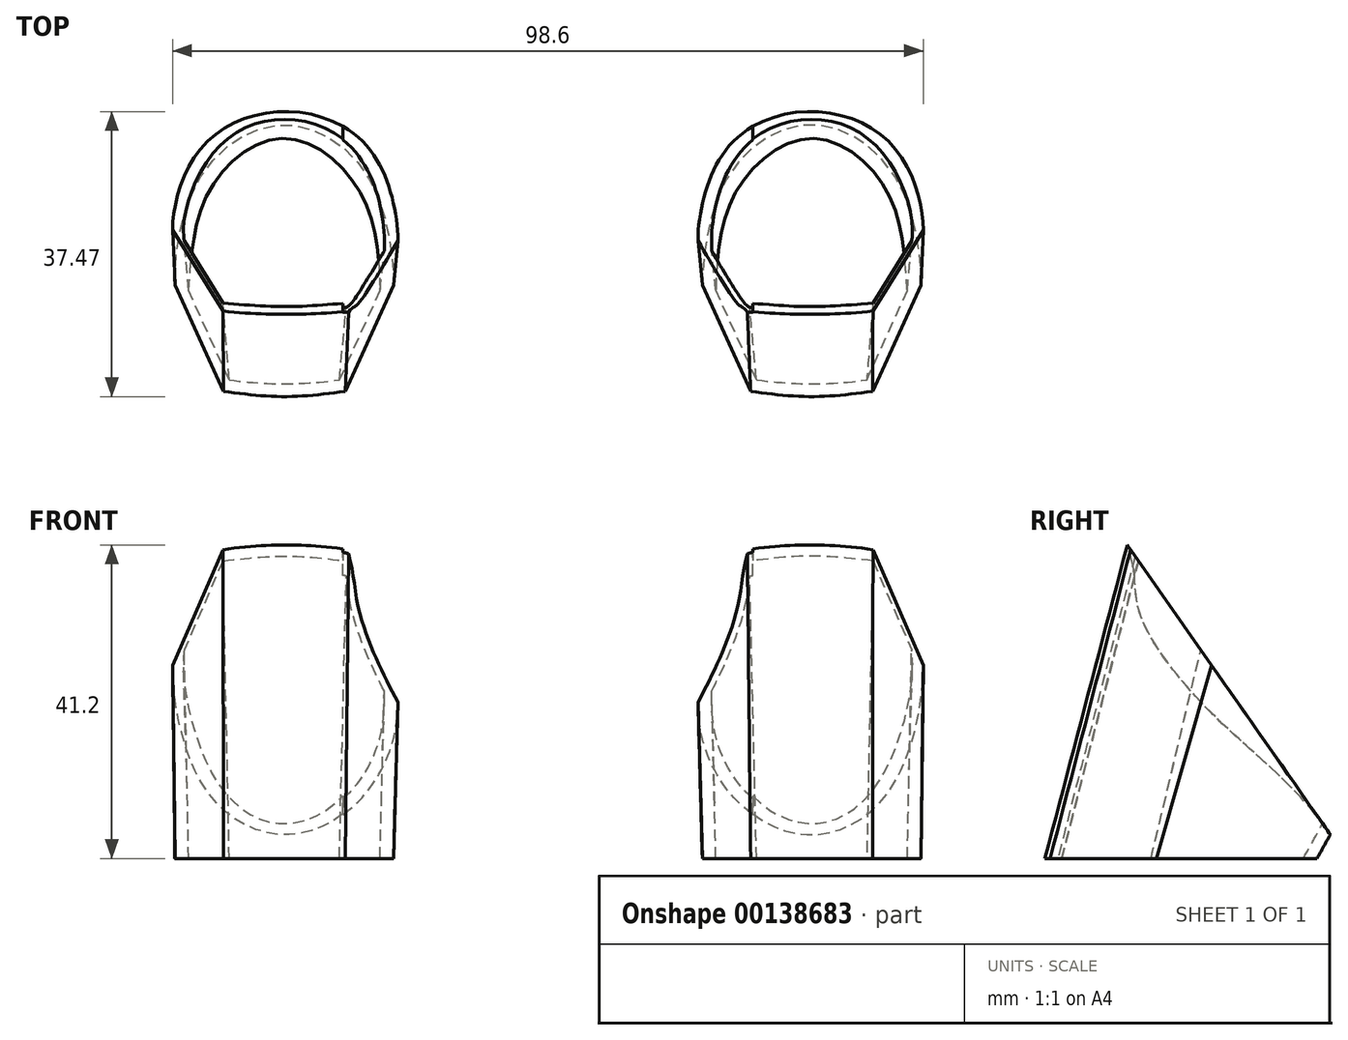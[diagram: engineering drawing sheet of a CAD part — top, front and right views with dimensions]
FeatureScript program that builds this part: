
annotation { "Feature Type Name" : "Feature", "Feature Type Description" : "" }
export const myFeature = defineFeature(function(context is Context, id is Id, definition is map)
    precondition{}
    {
        {
            var Q0;
            Q0=qCreatedBy(makeId("Top.planeOp"),FACE);
            var sketch = newSketch(context, id + "F0", { "sketchPlane" : qUnion([Q0])});
            skLineSegment(sketch, "E0", {"start": v(-1.23, -17.04) * mm, "end": v(5.12, -3.07) * mm});
            skLineSegment(sketch, "E1", {"start": v(-17.23, -17.04) * mm, "end": v(-23.58, -3.07) * mm});
            skPoint(sketch, "E2.2.internal.snap0", {"position": v(-9.23, -17.04) * mm});
            skFitSpline(sketch, "E2", {"points": [v(-23.58, -3.07) * mm, v(-20.66, 10.4) * mm, v(-9.23, 18.01) * mm, v(2.2, 10.4) * mm, v(5.12, -3.07) * mm], "startDerivative": vector(-1.89, 32.45) * mm, "endDerivative": vector(-0.1, -29.67) * mm});
            skFitSpline(sketch, "E3", {"points": [v(-17.23, -17.04) * mm, v(-9.23, -17.71) * mm, v(-1.23, -17.04) * mm], "startDerivative": vector(16.69, -2.01) * mm, "endDerivative": vector(16.69, 2.01) * mm});
            skLineSegment(sketch, "E4", {"start": v(10.38, -21.65) * mm, "end": v(-32.58, -21.65) * mm});
            skLineSegment(sketch, "E5", {"start": v(-40, 21.95) * mm, "end": v(17.74, 21.95) * mm});
            skSolve(sketch);
        }
        {
            var Q0;
            Q0=sQuery(id+"F0.wireOp",EDGE,"E5");
            cPlane(context, id + "F1", {"entities" : qUnion([Q0]), "cplaneType" : CPlaneType.LINE_ANGLE, "offset" : 25.4 * mm, "angle" : 35 * degree, "width" : 152.4 * mm, "height" : 152.4 * mm});
        }
        {
            var Q0;
            Q0=qCreatedBy(id+"F1.planeOp",FACE);
            var sketch = newSketch(context, id + "F2", { "sketchPlane" : qUnion([Q0])});
            skFitSpline(sketch, "E6", {"points": [v(-5.82, 18.4) * mm, v(-1.25, -1.92) * mm, v(9.18, -8.78) * mm, v(19.33, -1.92) * mm, v(23.9, 18.4) * mm], "startDerivative": vector(0, -61.98) * mm, "endDerivative": vector(0, 61.98) * mm});
            skLineSegment(sketch, "E7", {"start": v(-5.82, 18.4) * mm, "end": v(0.79, 36.94) * mm});
            skFitSpline(sketch, "E8", {"points": [v(0.79, 36.94) * mm, v(8.9, 37.7) * mm, v(17.3, 36.94) * mm], "startDerivative": vector(19.24, 3.46) * mm, "endDerivative": vector(17.7, -3.53) * mm});
            skLineSegment(sketch, "E9", {"start": v(23.9, 18.4) * mm, "end": v(17.3, 36.94) * mm});
            skLineSegment(sketch, "E10.0", {"start": v(40, -12.59) * mm, "end": v(-17.74, -12.59) * mm});
            skSolve(sketch);
        }
        {
            var Q0;
            Q0=makeQuery(id+"F0.imprint","IMPRINT",FACE,{"disambiguationData":[TD([[makeQuery(id+"F0.imprint","IMPRINT",EDGE,{"derivedFrom":sQuery(id+"F0.wireOp",EDGE,"E0")}),1.0]])]});
            var Q1;
            Q1=makeQuery(id+"F2.imprint","IMPRINT",FACE,{"disambiguationData":[TD([[makeQuery(id+"F2.imprint","IMPRINT",EDGE,{"derivedFrom":sQuery(id+"F2.wireOp",EDGE,"E6")}),1.0]])]});
            loft(context, id + "F3", {"sheetProfilesArray" : [{ "sheetProfileEntities" : qUnion([Q0]) }, { "sheetProfileEntities" : qUnion([Q1]) }]});
        }
        {
            var Q0;
            Q0=qCreatedBy(makeId("Top.planeOp"),FACE);
            var sketch = newSketch(context, id + "F4", { "sketchPlane" : qUnion([Q0])});
            skFitSpline(sketch, "E11.0.0", {"points": [v(-17.23, -17.04) * mm, v(-14.45, -17.38) * mm, v(-9.23, -18.05) * mm, v(-4.01, -17.38) * mm, v(-1.23, -17.04) * mm]});
            skLineSegment(sketch, "E11.0.1", {"start": v(-1.23, -17.04) * mm, "end": v(5.12, -3.07) * mm});
            skFitSpline(sketch, "E11.0.2", {"points": [v(5.12, -3.07) * mm, v(5.13, -0.6) * mm, v(4.22, 12.05) * mm, v(-9.25, 21.01) * mm, v(-22.6, 11.95) * mm, v(-23.74, -0.37) * mm, v(-23.58, -3.07) * mm]});
            skLineSegment(sketch, "E11.0.3", {"start": v(-23.58, -3.07) * mm, "end": v(-17.23, -17.04) * mm});
            skFitSpline(sketch, "E12", {"points": [v(-16.47, -15.52) * mm, v(-9.46, -16.03) * mm, v(-2, -15.52) * mm], "startDerivative": vector(14.42, -1.9) * mm, "endDerivative": vector(15.64, 1.87) * mm});
            skLineSegment(sketch, "E13", {"start": v(-2, -15.52) * mm, "end": v(3.34, -3.78) * mm});
            skLineSegment(sketch, "E14", {"start": v(-16.47, -15.52) * mm, "end": v(-21.8, -3.78) * mm});
            skFitSpline(sketch, "E15", {"points": [v(-21.8, -3.78) * mm, v(-19.26, 9) * mm, v(-9.23, 16.23) * mm, v(0.8, 9) * mm, v(3.34, -3.78) * mm], "startDerivative": vector(3.68, 44.37) * mm, "endDerivative": vector(1.43, -50.48) * mm});
            skPoint(sketch, "E16.0", {"position": v(-20.66, 10.4) * mm});
            skPoint(sketch, "E17.0", {"position": v(-9.23, 18.01) * mm});
            skPoint(sketch, "E18.0", {"position": v(2.2, 10.4) * mm});
            skSolve(sketch);
        }
        {
            var Q0;
            Q0=qCreatedBy(id+"F1.planeOp",FACE);
            var sketch = newSketch(context, id + "F5", { "sketchPlane" : qUnion([Q0])});
            skLineSegment(sketch, "E19.0", {"start": v(23.9, 18.4) * mm, "end": v(17.3, 36.94) * mm});
            skFitSpline(sketch, "E20.0", {"points": [v(17.83, 38.56) * mm, v(16.45, 38.83) * mm, v(14.96, 39.03) * mm, v(13.36, 39.16) * mm, v(12.65, 39.22) * mm, v(11.9, 39.26) * mm, v(11.14, 39.28) * mm, v(10.44, 39.3) * mm, v(9.71, 39.32) * mm, v(8.96, 39.32) * mm, v(8.22, 39.32) * mm, v(7.52, 39.3) * mm, v(6.85, 39.28) * mm, v(6.13, 39.25) * mm, v(5.42, 39.2) * mm, v(4.74, 39.15) * mm, v(4.01, 39.1) * mm, v(3.29, 39.01) * mm, v(2.56, 38.92) * mm, v(1.8, 38.82) * mm, v(1.04, 38.7) * mm, v(0.25, 38.56) * mm]});
            skFitSpline(sketch, "E21.0", {"points": [v(-6.86, 20.01) * mm, v(-6.86, 19.34) * mm, v(-6.85, 18.65) * mm, v(-6.82, 17.94) * mm, v(-6.8, 17.2) * mm, v(-6.75, 16.45) * mm, v(-6.69, 15.7) * mm, v(-6.62, 14.9) * mm, v(-6.54, 14.1) * mm, v(-6.45, 13.32) * mm, v(-6.35, 12.49) * mm, v(-6.23, 11.68) * mm, v(-6.1, 10.88) * mm, v(-5.95, 10.03) * mm, v(-5.79, 9.21) * mm, v(-5.61, 8.42) * mm, v(-5.42, 7.58) * mm, v(-5.22, 6.77) * mm, v(-4.99, 6) * mm, v(-4.75, 5.19) * mm, v(-4.5, 4.4) * mm, v(-4.22, 3.67) * mm, v(-3.93, 2.9) * mm, v(-3.62, 2.17) * mm, v(-3.28, 1.5) * mm, v(-2.94, 0.78) * mm, v(-2.57, 0.12) * mm, v(-2.18, -0.5) * mm, v(-1.78, -1.1) * mm, v(-1.35, -1.69) * mm, v(-0.9, -2.23) * mm, v(-0.44, -2.76) * mm, v(0.04, -3.26) * mm, v(0.55, -3.72) * mm, v(1.05, -4.17) * mm, v(1.57, -4.57) * mm, v(2.12, -4.94) * mm, v(2.65, -5.3) * mm, v(3.21, -5.63) * mm, v(3.78, -5.9) * mm, v(4.35, -6.18) * mm, v(4.93, -6.41) * mm, v(5.53, -6.6) * mm, v(6.12, -6.79) * mm, v(6.71, -6.93) * mm, v(7.31, -7.02) * mm, v(7.92, -7.12) * mm, v(8.52, -7.16) * mm, v(9.12, -7.16) * mm, v(9.73, -7.16) * mm, v(10.33, -7.12) * mm, v(10.93, -7.02) * mm, v(11.52, -6.93) * mm, v(12.11, -6.79) * mm, v(12.7, -6.6) * mm, v(13.28, -6.42) * mm, v(13.85, -6.18) * mm, v(14.41, -5.9) * mm, v(14.98, -5.63) * mm, v(15.52, -5.3) * mm, v(16.05, -4.94) * mm, v(16.66, -4.52) * mm, v(17.24, -4.05) * mm, v(17.8, -3.52) * mm, v(18.36, -2.98) * mm, v(18.88, -2.4) * mm, v(19.37, -1.76) * mm, v(19.75, -1.27) * mm, v(20.1, -0.76) * mm, v(20.42, -0.22) * mm, v(20.75, 0.31) * mm, v(21.05, 0.88) * mm, v(21.35, 1.5) * mm, v(21.68, 2.17) * mm, v(21.98, 2.9) * mm, v(22.27, 3.67) * mm, v(22.55, 4.4) * mm, v(22.8, 5.19) * mm, v(23.04, 6) * mm, v(23.27, 6.78) * mm, v(23.48, 7.58) * mm, v(23.67, 8.42) * mm, v(23.85, 9.22) * mm, v(24, 10.03) * mm, v(24.15, 10.88) * mm, v(24.3, 11.68) * mm, v(24.41, 12.5) * mm, v(24.51, 13.32) * mm, v(24.61, 14.1) * mm, v(24.7, 14.9) * mm, v(24.76, 15.7) * mm, v(24.82, 16.45) * mm, v(24.87, 17.2) * mm, v(24.9, 17.94) * mm, v(24.93, 18.65) * mm, v(24.94, 19.34) * mm, v(24.94, 20.01) * mm]});
            skLineSegment(sketch, "E22.0", {"start": v(0.79, 36.94) * mm, "end": v(-5.82, 18.4) * mm});
            skFitSpline(sketch, "E23", {"points": [v(17.3, 35.16) * mm, v(8.9, 35.93) * mm, v(1.05, 35.16) * mm], "startDerivative": vector(-16.31, 2.01) * mm, "endDerivative": vector(-16.4, -1.86) * mm});
            skPoint(sketch, "E24.0", {"position": v(9.23, 9.2) * mm});
            skPoint(sketch, "E25.0", {"position": v(8.9, 37.7) * mm});
            skLineSegment(sketch, "E26", {"start": v(1.05, 35.16) * mm, "end": v(-4.04, 20.88) * mm});
            skLineSegment(sketch, "E27", {"start": v(17.3, 35.16) * mm, "end": v(22.38, 20.88) * mm});
            skFitSpline(sketch, "E28", {"points": [v(22.38, 20.88) * mm, v(17.93, -0.52) * mm, v(9.18, -7) * mm, v(0.15, -0.52) * mm, v(-4.04, 20.88) * mm], "startDerivative": vector(6.23, -52.02) * mm, "endDerivative": vector(2.54, 68.04) * mm});
            skPoint(sketch, "E29.0", {"position": v(-1.25, -1.92) * mm});
            skPoint(sketch, "E30.0", {"position": v(9.18, -8.78) * mm});
            skPoint(sketch, "E31.0", {"position": v(19.33, -1.92) * mm});
            skSolve(sketch);
        }
        {
            var Q1;
            Q1=makeQuery(id+"F4.imprint","IMPRINT",FACE,{"disambiguationData":[TD([[makeQuery(id+"F4.imprint","IMPRINT",EDGE,{"derivedFrom":sQuery(id+"F4.wireOp",EDGE,"E12")}),1.0]])]});
            var Q2;
            Q2=makeQuery(id+"F5.imprint","IMPRINT",FACE,{"disambiguationData":[TD([[makeQuery(id+"F5.imprint","IMPRINT",EDGE,{"derivedFrom":sQuery(id+"F5.wireOp",EDGE,"E23")}),1.0]])]});
            loft(context, id + "F6", {"operationType" : NewBodyOperationType.REMOVE, "sheetProfilesArray" : [{ "sheetProfileEntities" : qUnion([Q1]) }, { "sheetProfileEntities" : qUnion([Q2]) }]});
        }
        {
            var Q0;
            Q0=qCreatedBy(makeId("Right.planeOp"),FACE);
            cPlane(context, id + "F7", {"entities" : qUnion([Q0]), "cplaneType" : CPlaneType.OFFSET, "offset" : 25.4 * mm, "width" : 152.4 * mm, "height" : 152.4 * mm});
        }
        {
            var Q0;
            Q0=qCreatedBy(id+"F7.planeOp",FACE);
            var sketch = newSketch(context, id + "F8", { "sketchPlane" : qUnion([Q0])});
            skLineSegment(sketch, "E32.0", {"start": v(4.17, 25.38) * mm, "end": v(-6.46, 40.57) * mm});
            skFitSpline(sketch, "E33", {"points": [v(-17.71, 0) * mm, v(-14.1, 13.73) * mm, v(-10.5, 27.47) * mm, v(-6.9, 41.2) * mm]});
            skFitSpline(sketch, "E34.0", {"points": [v(4.17, 25.38) * mm, v(4.91, 24.33) * mm, v(6.56, 21.97) * mm, v(9.31, 18.05) * mm, v(11.64, 14.72) * mm, v(13.4, 12.2) * mm, v(14.66, 10.4) * mm, v(15.81, 8.76) * mm, v(16.83, 7.31) * mm, v(17.7, 6.06) * mm, v(18.68, 4.66) * mm, v(19.53, 3.46) * mm, v(19.76, 3.12) * mm, v(19.76, 3.12) * mm]});
            skFitSpline(sketch, "E35", {"points": [v(19.76, 3.12) * mm, v(4.9, 18.36) * mm, v(-5.23, 32.12) * mm, v(-6.1, 38.14) * mm, v(-6.9, 41.2) * mm], "startDerivative": vector(-37.5, 55.42) * mm, "endDerivative": vector(-1.32, 12.1) * mm});
            skLineSegment(sketch, "E36", {"start": v(-6.46, 40.57) * mm, "end": v(-6.9, 41.2) * mm});
            skSolve(sketch);
        }
        {
            var Q0;
            Q0=makeQuery(id+"F8.imprint","IMPRINT",FACE,{"disambiguationData":[TD([[makeQuery(id+"F8.imprint","IMPRINT",EDGE,{"derivedFrom":sQuery(id+"F8.wireOp",EDGE,"E32.0")}),1.0]])]});
            extrude(context, id + "F9", {"entities" : qUnion([Q0]), "operationType" : NewBodyOperationType.REMOVE, "oppositeDirection" : true, "depth" : 26.92 * mm});
        }
        {
            var Q0;
            Q0=makeQuery(id+"F3.opLoft","SWEPT_BODY",BODY,{"disambiguationData":[OSD([makeQuery(id+"F0.imprint","IMPRINT",FACE,{"disambiguationData":[TD([[makeQuery(id+"F0.imprint","IMPRINT",EDGE,{"derivedFrom":sQuery(id+"F0.wireOp",EDGE,"E0")}),1.0]])]}),makeQuery(id+"F2.imprint","IMPRINT",FACE,{"disambiguationData":[TD([[makeQuery(id+"F2.imprint","IMPRINT",EDGE,{"derivedFrom":sQuery(id+"F2.wireOp",EDGE,"E6")}),1.0]])]})])]});
            var Q1;
            Q1=qCreatedBy(id+"F7.planeOp",FACE);
            mirror(context, id + "F10", {"entities" : qUnion([Q0]), "mirrorPlane" : qUnion([Q1])});
        }
    });
